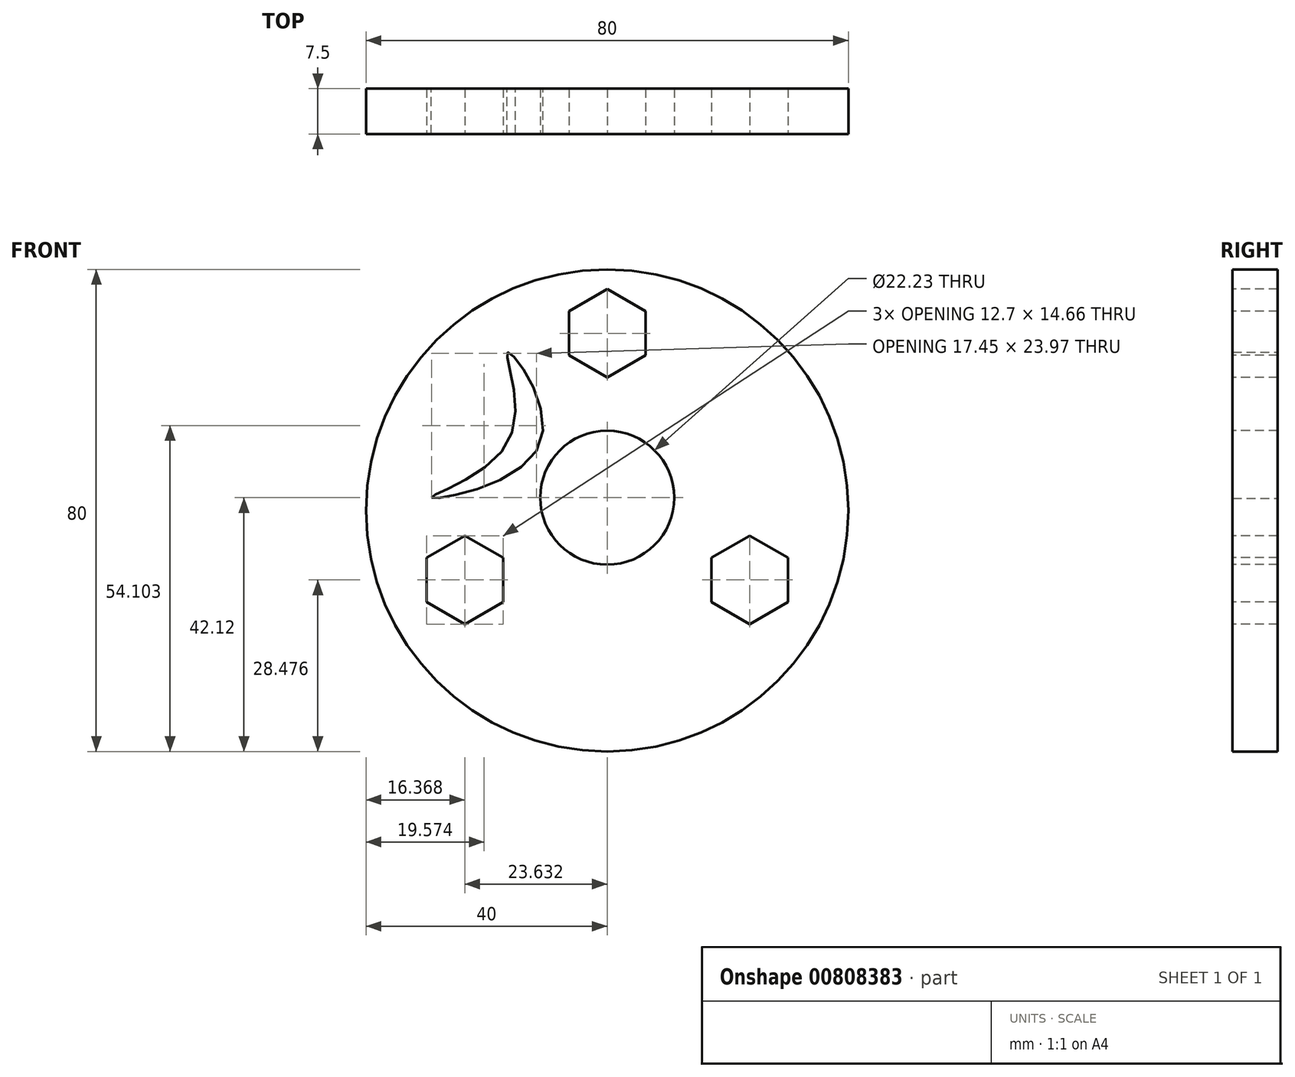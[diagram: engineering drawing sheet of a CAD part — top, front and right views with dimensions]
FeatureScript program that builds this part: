
annotation { "Feature Type Name" : "Feature", "Feature Type Description" : "" }
export const myFeature = defineFeature(function(context is Context, id is Id, definition is map)
    precondition{}
    {
        {
            var Q0;
            Q0=qCreatedBy(makeId("Front.planeOp"),FACE);
            var sketch = newSketch(context, id + "F0", { "sketchPlane" : qUnion([Q0])});
            skCircle(sketch, "E0", {"center": v(0, -2.12) * mm, "radius": 40 * mm});
            skSolve(sketch);
        }
        {
            var Q0;
            Q0 = qSketchRegion(id + "F0", true);
            extrude(context, id + "F1", {"entities" : qUnion([Q0]), "depth" : 7.5 * mm, "offsetDistance" : 25 * mm});
        }
        {
            var Q0;
            Q0=makeQuery(id+"F1.opExtrude","CAP_FACE",FACE,{"disambiguationData":[OSD([sQuery(id+"F0.wireOp",EDGE,"E0")])],"isStart":false});
            var sketch = newSketch(context, id + "F2", { "sketchPlane" : qUnion([Q0])});
            skCircle(sketch, "E1", {"center": v(0, 0) * mm, "radius": 11.11 * mm});
            skSolve(sketch);
        }
        {
            var Q0;
            Q0 = qSketchRegion(id + "F2", true);
            extrude(context, id + "F3", {"entities" : qUnion([Q0]), "operationType" : NewBodyOperationType.REMOVE, "oppositeDirection" : true, "depth" : 25 * mm, "offsetDistance" : 25 * mm});
        }
        {
            var Q0;
            Q0=makeQuery(id+"F1.opExtrude","CAP_FACE",FACE,{"disambiguationData":[OSD([sQuery(id+"F0.wireOp",EDGE,"E0")])],"isStart":false});
            var sketch = newSketch(context, id + "F4", { "sketchPlane" : qUnion([Q0])});
            skCircle(sketch, "E2.cCircle", {"center": v(0, 27.29) * mm, "radius": 6.35 * mm, "construction": true});
            skLineSegment(sketch, "E2.0", {"start": v(6.35, 30.95) * mm, "end": v(6.35, 23.62) * mm});
            skLineSegment(sketch, "E2.1", {"start": v(6.35, 23.62) * mm, "end": v(0, 19.96) * mm});
            skLineSegment(sketch, "E2.2", {"start": v(0, 19.96) * mm, "end": v(-6.35, 23.62) * mm});
            skLineSegment(sketch, "E2.3", {"start": v(-6.35, 23.62) * mm, "end": v(-6.35, 30.95) * mm});
            skLineSegment(sketch, "E2.4", {"start": v(-6.35, 30.95) * mm, "end": v(0, 34.62) * mm});
            skLineSegment(sketch, "E2.5", {"start": v(0, 34.62) * mm, "end": v(6.35, 30.95) * mm});
            skPoint(sketch, "E2.0.midPoint", {"position": v(6.35, 27.29) * mm});
            skCircle(sketch, "E3.1.0", {"center": v(-23.63, -13.64) * mm, "radius": 6.35 * mm, "construction": true});
            skCircle(sketch, "E3.2.0", {"center": v(23.63, -13.64) * mm, "radius": 6.35 * mm, "construction": true});
            skPoint(sketch, "E3.center", {"position": v(0, 0) * mm});
            skLineSegment(sketch, "E4.0", {"start": v(29.98, -9.98) * mm, "end": v(29.98, -17.31) * mm});
            skLineSegment(sketch, "E4.1", {"start": v(29.98, -17.31) * mm, "end": v(23.63, -20.98) * mm});
            skLineSegment(sketch, "E4.2", {"start": v(23.63, -20.98) * mm, "end": v(17.28, -17.31) * mm});
            skLineSegment(sketch, "E4.3", {"start": v(17.28, -17.31) * mm, "end": v(17.28, -9.98) * mm});
            skLineSegment(sketch, "E4.4", {"start": v(17.28, -9.98) * mm, "end": v(23.63, -6.31) * mm});
            skLineSegment(sketch, "E4.5", {"start": v(23.63, -6.31) * mm, "end": v(29.98, -9.98) * mm});
            skPoint(sketch, "E4.0.midPoint", {"position": v(29.98, -13.64) * mm});
            skLineSegment(sketch, "E5.0", {"start": v(-17.28, -9.98) * mm, "end": v(-17.28, -17.31) * mm});
            skLineSegment(sketch, "E5.1", {"start": v(-17.28, -17.31) * mm, "end": v(-23.63, -20.98) * mm});
            skLineSegment(sketch, "E5.2", {"start": v(-23.63, -20.98) * mm, "end": v(-29.98, -17.31) * mm});
            skLineSegment(sketch, "E5.3", {"start": v(-29.98, -17.31) * mm, "end": v(-29.98, -9.98) * mm});
            skLineSegment(sketch, "E5.4", {"start": v(-29.98, -9.98) * mm, "end": v(-23.63, -6.31) * mm});
            skLineSegment(sketch, "E5.5", {"start": v(-23.63, -6.31) * mm, "end": v(-17.28, -9.98) * mm});
            skPoint(sketch, "E5.0.midPoint", {"position": v(-17.28, -13.64) * mm});
            skSolve(sketch);
        }
        {
            var Q0;
            Q0 = qSketchRegion(id + "F4", true);
            extrude(context, id + "F5", {"entities" : qUnion([Q0]), "operationType" : NewBodyOperationType.REMOVE, "oppositeDirection" : true, "depth" : 25 * mm, "offsetDistance" : 25 * mm});
        }
        {
            var Q0;
            Q0=makeQuery(id+"F1.opExtrude","CAP_FACE",FACE,{"disambiguationData":[OSD([sQuery(id+"F0.wireOp",EDGE,"E0")])],"isStart":false});
            var sketch = newSketch(context, id + "F6", { "sketchPlane" : qUnion([Q0])});
            skFitSpline(sketch, "E6", {"points": [v(-29.15, 0) * mm, v(-11.22, 8.7) * mm, v(-16.45, 24.14) * mm, v(-16.2, 9.7) * mm, v(-29.15, 0) * mm]});
            skSolve(sketch);
        }
        {
            var Q0;
            Q0 = qSketchRegion(id + "F6", true);
            extrude(context, id + "F7", {"entities" : qUnion([Q0]), "operationType" : NewBodyOperationType.REMOVE, "oppositeDirection" : true, "depth" : 25 * mm, "offsetDistance" : 25 * mm});
        }
    });
